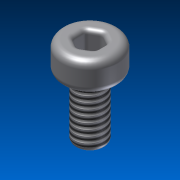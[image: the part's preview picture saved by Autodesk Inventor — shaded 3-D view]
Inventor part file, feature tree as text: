
AUTODESK INVENTOR PART (.ipt)
format: ipt  version: 2013 (Build 170138000, 138)  size: 181,760 bytes
history: native  units: mm
features: extrude x3, sketch x3, fillet x2, other x1, thread x1
ambient origin geometry x1: Origin
feature tree (10):
  other  "ソリッド1"
  extrude  "押し出し1"  Depth=3.8mm
  extrude  "押し出し2"  Depth=2.0mm TaperAngle=0.0deg
  extrude  "押し出し3"  Depth=2.0mm
  fillet  "フィレット1"  Radius=4.0mm
  fillet  "フィレット2"  Radius=0.75mm
  thread  "ねじ3"
  sketch  "スケッチ1"
  sketch  "スケッチ2"
  sketch  "スケッチ3"
